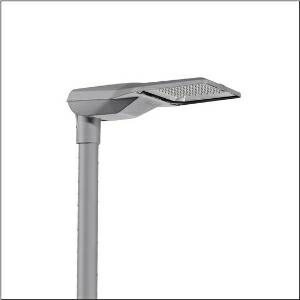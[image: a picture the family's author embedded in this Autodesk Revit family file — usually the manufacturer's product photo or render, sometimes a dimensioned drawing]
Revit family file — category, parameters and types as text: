
# Revit family: streetlight_sl_21_iq_midi___st0_5a_5xe3b41g08mb_6195
name_source: partatom
category: Lighting Fixtures
units: mm (PartAtom-declared; Revit-internal decimal feet)

## family parameters
Cut with Voids When Loaded = No
Host = Face
Light Source = No
Part Type = Normal
Room Calculation Point = No
Round Connector Dimension = Use Diameter
Shared = No

## types (1)
- --- (1 x LED, 20360 lm, 146.7 W, 4000K)
    Apparent Load = 147 VA
    CIE Flux Codes = 41 75 97 100 100
    Color Rendering = 70
    Color Temperature = 4000K
    Default Elevation = 1800 mm
    Description = Streetlight SL 21 iQ midi, mast luminaire, primary light control with lens, of PMMA, primary optical cover: cover, of toughened safety glass, transparent, light distribution: ST0.5a, light emission: direct distribution, primary light characteristic: asymmetric, installation type: post-top, side-entry, LED, High Power LED, rated luminous flux: 20.360lm, luminous efficacy: 139lm/W, light colour: 740, colour temperature: 4000K, control gear: iQ Street-Remote, control: Street-Remote, Auto-Match, Temp-Guard, Lumen-Switch, Night-Set, Smart-Wire, Light-Fading, Desk-Remote (wireless, voltage-free reading and setting of iQ features in the workshop via application-optimized NFC function/RFID function), optimised constant luminous flux control (CLO 2.0), pre-setting: linear dimming characteristic, mains connection: 230..240V, AC, 50/60Hz, start of lifetime: 147W, end of service life: 161W, reduction: 62W, luminaire housing, of diecast aluminium, powder-coated, SITECO metallic grey (DB 702S), corrosivity category C5 high according to DIN EN ISO 12944, please order mast flange separately, inclination adjustable: 0°, 5°, 10°, 15°, sealing non-destructively replaceable, multi-level sealing system, length: 644mm, width: 335mm, height: 110mm, mast flange for spigot size: 42mm (side-entry): 5XC10008XM4, 60/48mm (side-entry/post-top): 5XC10108XM2, 76/60mm (side-entry/post-top): 5XC10108XM1, mounting height: 4..8m, protection rating (complete): IP66, insulation class (complete): insulation class II (safety insulation), certification: CE, ENEC, ENEC+, VDE, impact resistance: IK10, permissible operating ambient temperature for outdoor applications: -40..+50°C, standard-compliant lighting for roads and squares, packaging unit: 1 piece

Light Distribution: ST0.5a
    Height = 111 mm
    Lamp = 1 x LED
    Lamp Light Flux = 20360 lm
    Lamp Power = 146.7 W
    Lamp count = 1
    Length = 644 mm
    Luminous efficacy = 139 lm/W
    Manufacturer = Siteco
    ModVariant = No
    Model = 5XE3B41G08MB
    Number of Poles = 1
    OnlyDefault = Yes
    Power Factor = 1
    Product Name = Streetlight SL 21 iQ midi | ST0.5a
    Product group = mast luminaire | pylon top
    ProductGroupID = 6100
    Protection Class = Protection class II
    Protection Degree = IP 66
    RLX_Detail_Level = 1
    RLX_Emergency_Light_Flux = 0 lm
    RLX_Emergency_Type = 0
    RLX_Emergency_Type_DB = No
    RlxData = <blob elided: 37961 chars, md5=f093039d>
    Socket = socket
    Standby Power = 0 W
    System Light Flux = 20360 lm
    System Power = 147 W
    Type Comments = factory setting: luminous flux: 100 % | dim-lin: 254 | 753 mA
    Type Image = l_1004298.jpg
    URL = http://relux.com
    VarID = @adj_189223
    Voltage = 0 V
    Weight = 0.00 kg
    Width = 336 mm

## geometry (parser evidence)
native form markers: Blend x4, Sweep x10
no freeform markers — native parametric forms only
